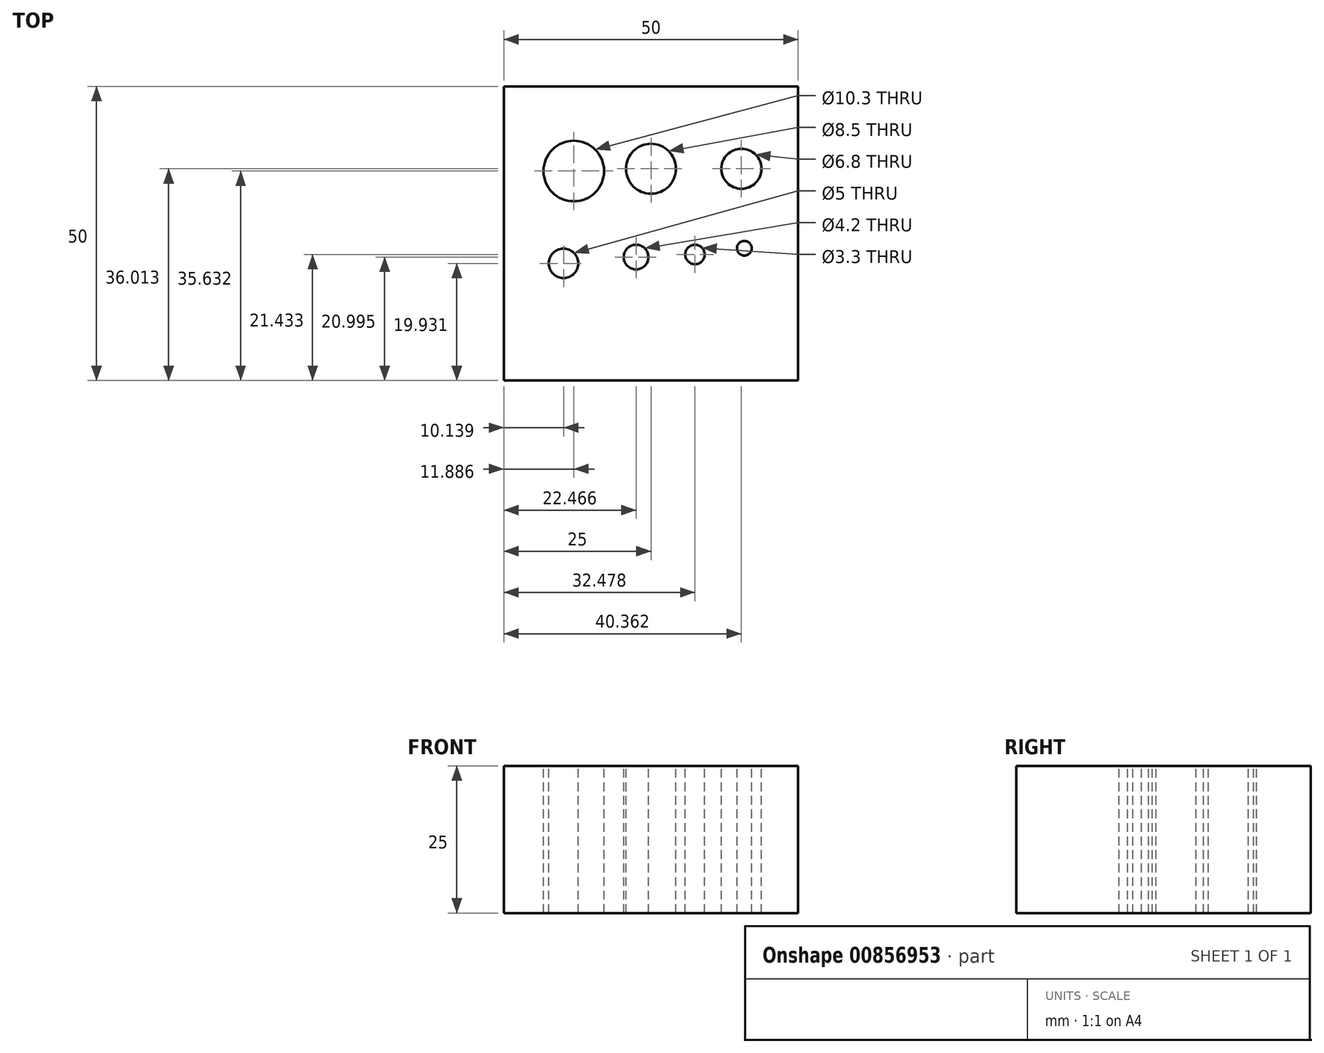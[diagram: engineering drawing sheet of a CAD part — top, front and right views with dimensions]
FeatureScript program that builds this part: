
annotation { "Feature Type Name" : "Feature", "Feature Type Description" : "" }
export const myFeature = defineFeature(function(context is Context, id is Id, definition is map)
    precondition{}
    {
        {
            var Q0;
            Q0=qCreatedBy(makeId("Top.planeOp"),FACE);
            var sketch = newSketch(context, id + "F0", { "sketchPlane" : qUnion([Q0])});
            skLineSegment(sketch, "E0.bottom", {"start": v(25, 25) * mm, "end": v(-25, 25) * mm});
            skLineSegment(sketch, "E0.top", {"start": v(25, -25) * mm, "end": v(-25, -25) * mm});
            skLineSegment(sketch, "E0.left", {"start": v(25, 25) * mm, "end": v(25, -25) * mm});
            skLineSegment(sketch, "E0.right", {"start": v(-25, 25) * mm, "end": v(-25, -25) * mm});
            skPoint(sketch, "E0.middle", {"position": v(0, 0) * mm});
            skSolve(sketch);
        }
        {
            var Q0;
            Q0 = qSketchRegion(id + "F0", true);
            extrude(context, id + "F1", {"entities" : qUnion([Q0]), "depth" : 25 * mm, "offsetDistance" : 25 * mm});
        }
        {
            var Q0;
            Q0=makeQuery(id+"F1.opExtrude","CAP_FACE",FACE,{"disambiguationData":[OSD([sQuery(id+"F0.wireOp",EDGE,"E0.bottom"),sQuery(id+"F0.wireOp",EDGE,"E0.top"),sQuery(id+"F0.wireOp",EDGE,"E0.left"),sQuery(id+"F0.wireOp",EDGE,"E0.right")])],"isStart":false});
            var sketch = newSketch(context, id + "F2", { "sketchPlane" : qUnion([Q0])});
            skPoint(sketch, "E1", {"position": v(-13.11, 10.63) * mm});
            skPoint(sketch, "E2", {"position": v(0, 11.01) * mm});
            skPoint(sketch, "E3", {"position": v(15.36, 11.01) * mm});
            skPoint(sketch, "E4", {"position": v(-14.86, -5.07) * mm});
            skPoint(sketch, "E5", {"position": v(-2.53, -4) * mm});
            skPoint(sketch, "E6", {"position": v(7.48, -3.57) * mm});
            skPoint(sketch, "E7", {"position": v(15.86, -2.5) * mm});
            skSolve(sketch);
        }
        {
            var Q0;
            Q0=sQuery(id+"F2.wireOp",VERTEX,"E1");
            var Q1;
            Q1=makeQuery(id+"F1.opExtrude","SWEPT_BODY",BODY,{"disambiguationData":[OSD([sQuery(id+"F0.wireOp",EDGE,"E0.bottom"),sQuery(id+"F0.wireOp",EDGE,"E0.top"),sQuery(id+"F0.wireOp",EDGE,"E0.left"),sQuery(id+"F0.wireOp",EDGE,"E0.right")])]});
            hole(context, id + "F3", {"style" : HoleStyle.SIMPLE, "endStyle" : HoleEndStyle.THROUGH, "standardTappedOrClearance" : lookupTablePath({ "standard" : "ISO", "engagement" : "75%", "pitch" : "1.75 mm", "size" : "M12", "type" : "Tapped" }), "standardBlindInLast" : lookupTablePath({ "standard" : "ISO", "engagement" : "75%", "pitch" : "1.75 mm", "size" : "M12", "type" : "Tapped" }), "holeDiameter" : 10.3 * mm, "majorDiameter" : 12 * mm, "showTappedDepth" : true, "isTappedThrough" : true, "tappedDepth" : 12 * mm, "tapClearance" : 3, "startFromSketch" : true, "locations" : qUnion([Q0]), "scope" : qUnion([Q1])});
        }
        {
            var Q0;
            Q0=sQuery(id+"F2.wireOp",VERTEX,"E2");
            var Q1;
            Q1=makeQuery(id+"F1.opExtrude","SWEPT_BODY",BODY,{"disambiguationData":[OSD([sQuery(id+"F0.wireOp",EDGE,"E0.bottom"),sQuery(id+"F0.wireOp",EDGE,"E0.top"),sQuery(id+"F0.wireOp",EDGE,"E0.left"),sQuery(id+"F0.wireOp",EDGE,"E0.right")])]});
            hole(context, id + "F4", {"style" : HoleStyle.SIMPLE, "endStyle" : HoleEndStyle.THROUGH, "standardTappedOrClearance" : lookupTablePath({ "standard" : "ISO", "engagement" : "75%", "pitch" : "1.5 mm", "size" : "M10", "type" : "Tapped" }), "standardBlindInLast" : lookupTablePath({ "standard" : "ISO", "engagement" : "75%", "pitch" : "1.5 mm", "size" : "M10", "type" : "Tapped" }), "holeDiameter" : 8.5 * mm, "majorDiameter" : 10 * mm, "showTappedDepth" : true, "isTappedThrough" : true, "tappedDepth" : 12 * mm, "tapClearance" : 3, "startFromSketch" : true, "locations" : qUnion([Q0]), "scope" : qUnion([Q1])});
        }
        {
            var Q0;
            Q0=sQuery(id+"F2.wireOp",VERTEX,"E3");
            var Q1;
            Q1=makeQuery(id+"F1.opExtrude","SWEPT_BODY",BODY,{"disambiguationData":[OSD([sQuery(id+"F0.wireOp",EDGE,"E0.bottom"),sQuery(id+"F0.wireOp",EDGE,"E0.top"),sQuery(id+"F0.wireOp",EDGE,"E0.left"),sQuery(id+"F0.wireOp",EDGE,"E0.right")])]});
            hole(context, id + "F5", {"style" : HoleStyle.SIMPLE, "endStyle" : HoleEndStyle.THROUGH, "standardTappedOrClearance" : lookupTablePath({ "standard" : "ISO", "engagement" : "75%", "pitch" : "1.25 mm", "size" : "M8", "type" : "Tapped" }), "standardBlindInLast" : lookupTablePath({ "standard" : "ISO", "engagement" : "75%", "pitch" : "1.25 mm", "size" : "M8", "type" : "Tapped" }), "holeDiameter" : 6.8 * mm, "majorDiameter" : 8 * mm, "showTappedDepth" : true, "isTappedThrough" : true, "tappedDepth" : 12 * mm, "tapClearance" : 3, "startFromSketch" : true, "locations" : qUnion([Q0]), "scope" : qUnion([Q1])});
        }
        {
            var Q0;
            Q0=sQuery(id+"F2.wireOp",VERTEX,"E4");
            var Q1;
            Q1=makeQuery(id+"F1.opExtrude","SWEPT_BODY",BODY,{"disambiguationData":[OSD([sQuery(id+"F0.wireOp",EDGE,"E0.bottom"),sQuery(id+"F0.wireOp",EDGE,"E0.top"),sQuery(id+"F0.wireOp",EDGE,"E0.left"),sQuery(id+"F0.wireOp",EDGE,"E0.right")])]});
            hole(context, id + "F6", {"style" : HoleStyle.SIMPLE, "endStyle" : HoleEndStyle.THROUGH, "standardTappedOrClearance" : lookupTablePath({ "standard" : "ISO", "engagement" : "75%", "pitch" : "1 mm", "size" : "M6", "type" : "Tapped" }), "standardBlindInLast" : lookupTablePath({ "standard" : "ISO", "engagement" : "75%", "pitch" : "1 mm", "size" : "M6", "type" : "Tapped" }), "holeDiameter" : 5 * mm, "majorDiameter" : 6 * mm, "showTappedDepth" : true, "isTappedThrough" : true, "tappedDepth" : 12 * mm, "tapClearance" : 3, "startFromSketch" : true, "locations" : qUnion([Q0]), "scope" : qUnion([Q1])});
        }
        {
            var Q0;
            Q0=sQuery(id+"F2.wireOp",VERTEX,"E5");
            var Q1;
            Q1=makeQuery(id+"F1.opExtrude","SWEPT_BODY",BODY,{"disambiguationData":[OSD([sQuery(id+"F0.wireOp",EDGE,"E0.bottom"),sQuery(id+"F0.wireOp",EDGE,"E0.top"),sQuery(id+"F0.wireOp",EDGE,"E0.left"),sQuery(id+"F0.wireOp",EDGE,"E0.right")])]});
            hole(context, id + "F7", {"style" : HoleStyle.SIMPLE, "endStyle" : HoleEndStyle.THROUGH, "standardTappedOrClearance" : lookupTablePath({ "standard" : "ISO", "engagement" : "75%", "pitch" : "0.8 mm", "size" : "M5", "type" : "Tapped" }), "standardBlindInLast" : lookupTablePath({ "standard" : "ISO", "engagement" : "75%", "pitch" : "0.8 mm", "size" : "M5", "type" : "Tapped" }), "holeDiameter" : 4.2 * mm, "majorDiameter" : 5 * mm, "showTappedDepth" : true, "isTappedThrough" : true, "tappedDepth" : 12 * mm, "tapClearance" : 3, "startFromSketch" : true, "locations" : qUnion([Q0]), "scope" : qUnion([Q1])});
        }
        {
            var Q0;
            Q0=sQuery(id+"F2.wireOp",VERTEX,"E6");
            var Q1;
            Q1=makeQuery(id+"F1.opExtrude","SWEPT_BODY",BODY,{"disambiguationData":[OSD([sQuery(id+"F0.wireOp",EDGE,"E0.bottom"),sQuery(id+"F0.wireOp",EDGE,"E0.top"),sQuery(id+"F0.wireOp",EDGE,"E0.left"),sQuery(id+"F0.wireOp",EDGE,"E0.right")])]});
            hole(context, id + "F8", {"style" : HoleStyle.SIMPLE, "endStyle" : HoleEndStyle.THROUGH, "standardTappedOrClearance" : lookupTablePath({ "standard" : "ISO", "engagement" : "75%", "pitch" : "0.7 mm", "size" : "M4", "type" : "Tapped" }), "standardBlindInLast" : lookupTablePath({ "standard" : "ISO", "engagement" : "75%", "pitch" : "0.7 mm", "size" : "M4", "type" : "Tapped" }), "holeDiameter" : 3.3 * mm, "majorDiameter" : 4 * mm, "showTappedDepth" : true, "isTappedThrough" : true, "tappedDepth" : 12 * mm, "tapClearance" : 3, "startFromSketch" : true, "locations" : qUnion([Q0]), "scope" : qUnion([Q1])});
        }
        {
            var Q0;
            Q0=sQuery(id+"F2.wireOp",VERTEX,"E7");
            var Q1;
            Q1=makeQuery(id+"F1.opExtrude","SWEPT_BODY",BODY,{"disambiguationData":[OSD([sQuery(id+"F0.wireOp",EDGE,"E0.bottom"),sQuery(id+"F0.wireOp",EDGE,"E0.top"),sQuery(id+"F0.wireOp",EDGE,"E0.left"),sQuery(id+"F0.wireOp",EDGE,"E0.right")])]});
            hole(context, id + "F9", {"style" : HoleStyle.SIMPLE, "endStyle" : HoleEndStyle.THROUGH, "standardTappedOrClearance" : lookupTablePath({ "standard" : "ISO", "engagement" : "75%", "pitch" : "0.5 mm", "size" : "M3", "type" : "Tapped" }), "standardBlindInLast" : lookupTablePath({ "standard" : "ISO", "engagement" : "75%", "pitch" : "0.5 mm", "size" : "M3", "type" : "Tapped" }), "holeDiameter" : 2.5 * mm, "majorDiameter" : 3 * mm, "showTappedDepth" : true, "isTappedThrough" : true, "tappedDepth" : 12 * mm, "tapClearance" : 3, "startFromSketch" : true, "locations" : qUnion([Q0]), "scope" : qUnion([Q1])});
        }
    });
